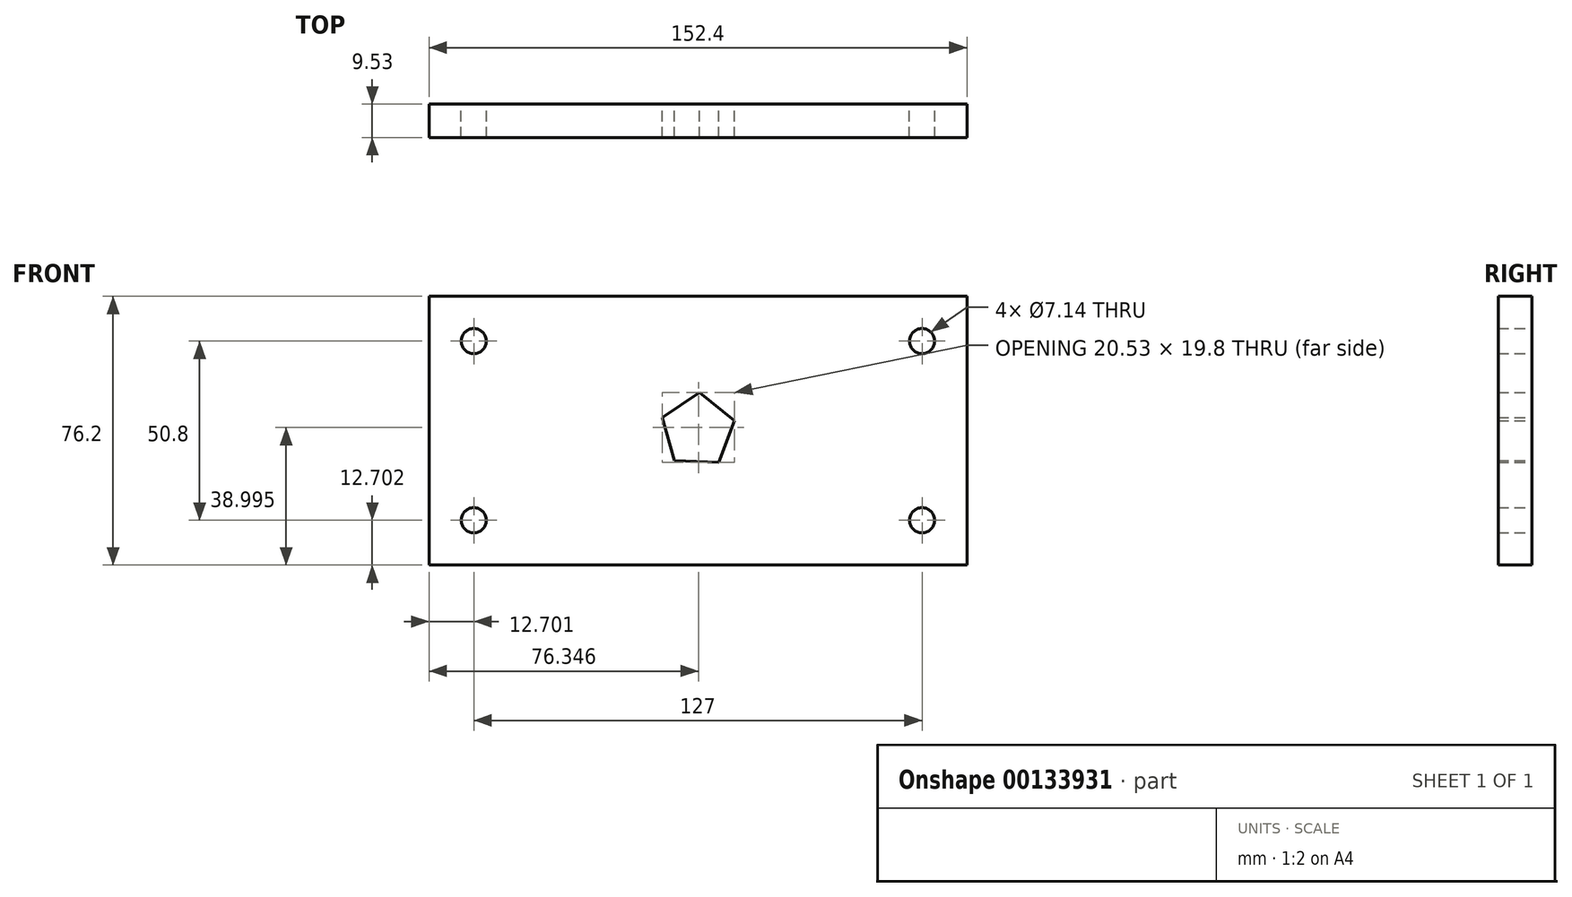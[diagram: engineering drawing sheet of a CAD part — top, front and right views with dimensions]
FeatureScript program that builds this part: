
annotation { "Feature Type Name" : "Feature", "Feature Type Description" : "" }
export const myFeature = defineFeature(function(context is Context, id is Id, definition is map)
    precondition{}
    {
        {
            var Q0;
            Q0=qCreatedBy(makeId("Front.planeOp"),FACE);
            var sketch = newSketch(context, id + "F0", { "sketchPlane" : qUnion([Q0])});
            skLineSegment(sketch, "E0.bottom", {"start": v(-92.35, 21.13) * mm, "end": v(60.05, 21.13) * mm});
            skLineSegment(sketch, "E0.top", {"start": v(-92.35, -55.07) * mm, "end": v(60.05, -55.07) * mm});
            skLineSegment(sketch, "E0.left", {"start": v(-92.35, 21.13) * mm, "end": v(-92.35, -55.07) * mm});
            skLineSegment(sketch, "E0.right", {"start": v(60.05, 21.13) * mm, "end": v(60.05, -55.07) * mm});
            skCircle(sketch, "E1", {"center": v(-79.65, -42.37) * mm, "radius": 3.57 * mm});
            skCircle(sketch, "E2", {"center": v(-79.65, 8.43) * mm, "radius": 3.57 * mm});
            skCircle(sketch, "E3", {"center": v(47.35, 8.43) * mm, "radius": 3.57 * mm});
            skCircle(sketch, "E4", {"center": v(47.35, -42.37) * mm, "radius": 3.57 * mm});
            skCircle(sketch, "E5.cCircle", {"center": v(-16.15, -16.97) * mm, "radius": 8.74 * mm, "construction": true});
            skLineSegment(sketch, "E5.0", {"start": v(-15.68, -6.18) * mm, "end": v(-5.74, -14.08) * mm});
            skLineSegment(sketch, "E5.1", {"start": v(-5.74, -14.08) * mm, "end": v(-10.18, -25.98) * mm});
            skLineSegment(sketch, "E5.2", {"start": v(-10.18, -25.98) * mm, "end": v(-22.87, -25.42) * mm});
            skLineSegment(sketch, "E5.3", {"start": v(-22.87, -25.42) * mm, "end": v(-26.27, -13.19) * mm});
            skLineSegment(sketch, "E5.4", {"start": v(-26.27, -13.19) * mm, "end": v(-15.68, -6.18) * mm});
            skPoint(sketch, "E5.0.midPoint", {"position": v(-10.7, -10.13) * mm});
            skSolve(sketch);
        }
        {
            var Q0;
            Q0=makeQuery(id+"F0.imprint","IMPRINT",FACE,{"disambiguationData":[TD([[makeQuery(id+"F0.imprint","IMPRINT",EDGE,{"derivedFrom":sQuery(id+"F0.wireOp",EDGE,"E0.bottom")}),-1.0]])]});
            extrude(context, id + "F1", {"entities" : qUnion([Q0]), "depth" : 9.52 * mm});
        }
    });
